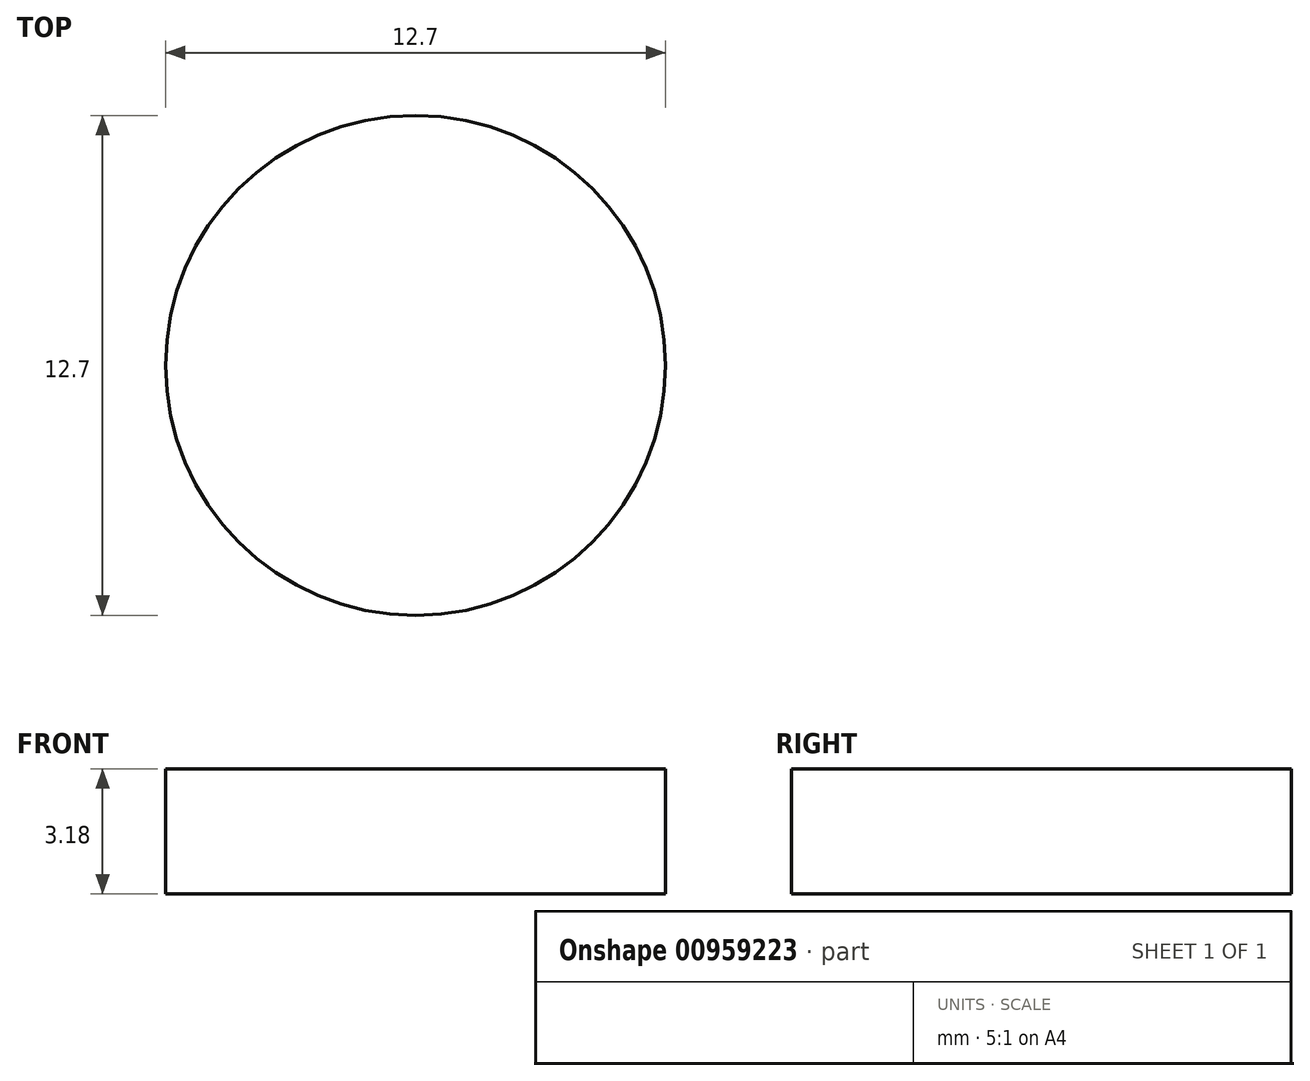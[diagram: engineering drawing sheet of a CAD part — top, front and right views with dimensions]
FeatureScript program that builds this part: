
annotation { "Feature Type Name" : "Feature", "Feature Type Description" : "" }
export const myFeature = defineFeature(function(context is Context, id is Id, definition is map)
    precondition{}
    {
        {
            var Q0;
            Q0=qCreatedBy(makeId("Top.planeOp"),FACE);
            var sketch = newSketch(context, id + "F0", { "sketchPlane" : qUnion([Q0])});
            skCircle(sketch, "E0", {"center": v(0, 0) * mm, "radius": 6.35 * mm});
            skSolve(sketch);
        }
        {
            var Q0;
            Q0=makeQuery(id+"F0.imprint","IMPRINT",FACE,{"disambiguationData":[TD([[makeQuery(id+"F0.imprint","IMPRINT",EDGE,{"derivedFrom":sQuery(id+"F0.wireOp",EDGE,"E0")}),1.0]])]});
            extrude(context, id + "F1", {"entities" : qUnion([Q0]), "depth" : 3.17 * mm, "offsetDistance" : 25.4 * mm});
        }
    });
